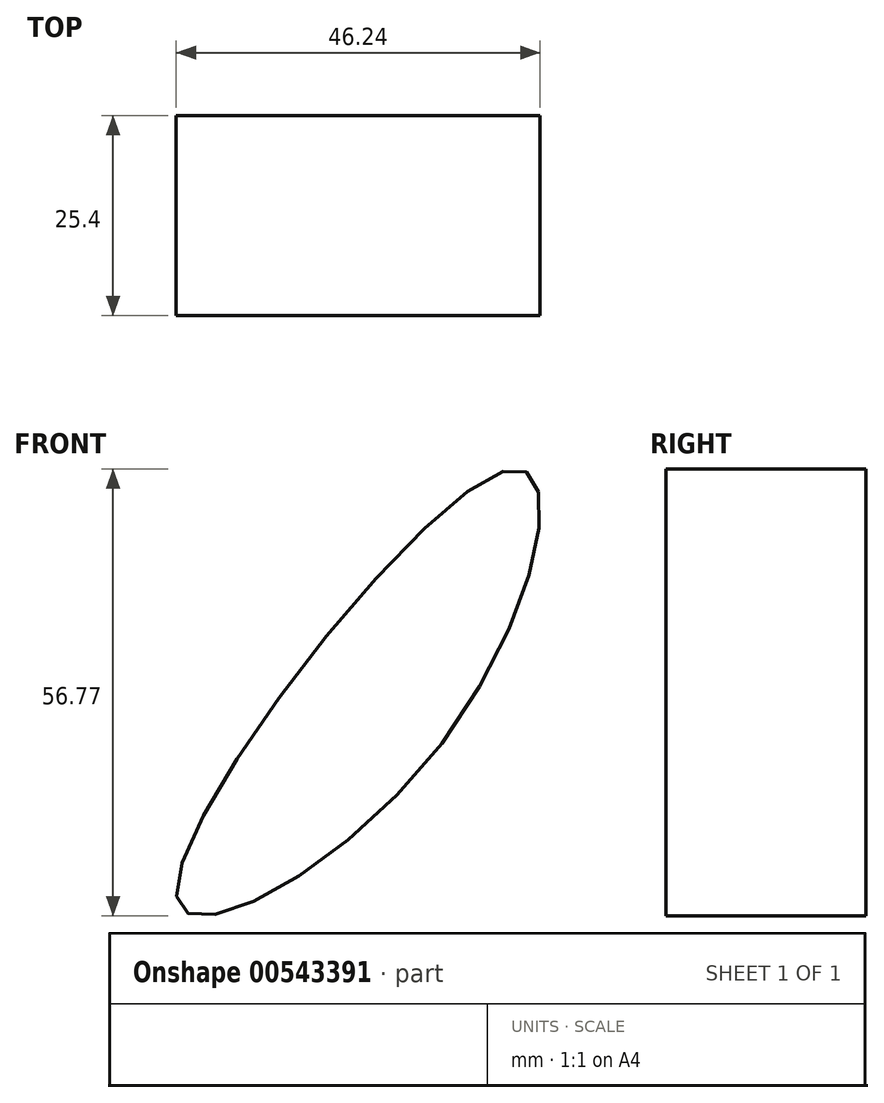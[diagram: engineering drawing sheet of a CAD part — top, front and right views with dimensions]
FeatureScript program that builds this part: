
annotation { "Feature Type Name" : "Feature", "Feature Type Description" : "" }
export const myFeature = defineFeature(function(context is Context, id is Id, definition is map)
    precondition{}
    {
        {
            var Q0;
            Q0=qCreatedBy(makeId("Front.planeOp"),FACE);
            var sketch = newSketch(context, id + "F0", { "sketchPlane" : qUnion([Q0])});
            skFitSpline(sketch, "E0", {"points": [v(0, 0) * mm, v(33.57, 19.24) * mm, v(42.54, 54.26) * mm, v(0, 0) * mm]});
            skSolve(sketch);
        }
        {
            var Q0;
            Q0=makeQuery(id+"F0.imprint","IMPRINT",FACE,{"disambiguationData":[TD([[makeQuery(id+"F0.imprint","IMPRINT",EDGE,{"derivedFrom":sQuery(id+"F0.wireOp",EDGE,"E0")}),1.0]])]});
            extrude(context, id + "F1", {"entities" : qUnion([Q0]), "depth" : 25.4 * mm, "offsetDistance" : 25.4 * mm});
        }
    });
